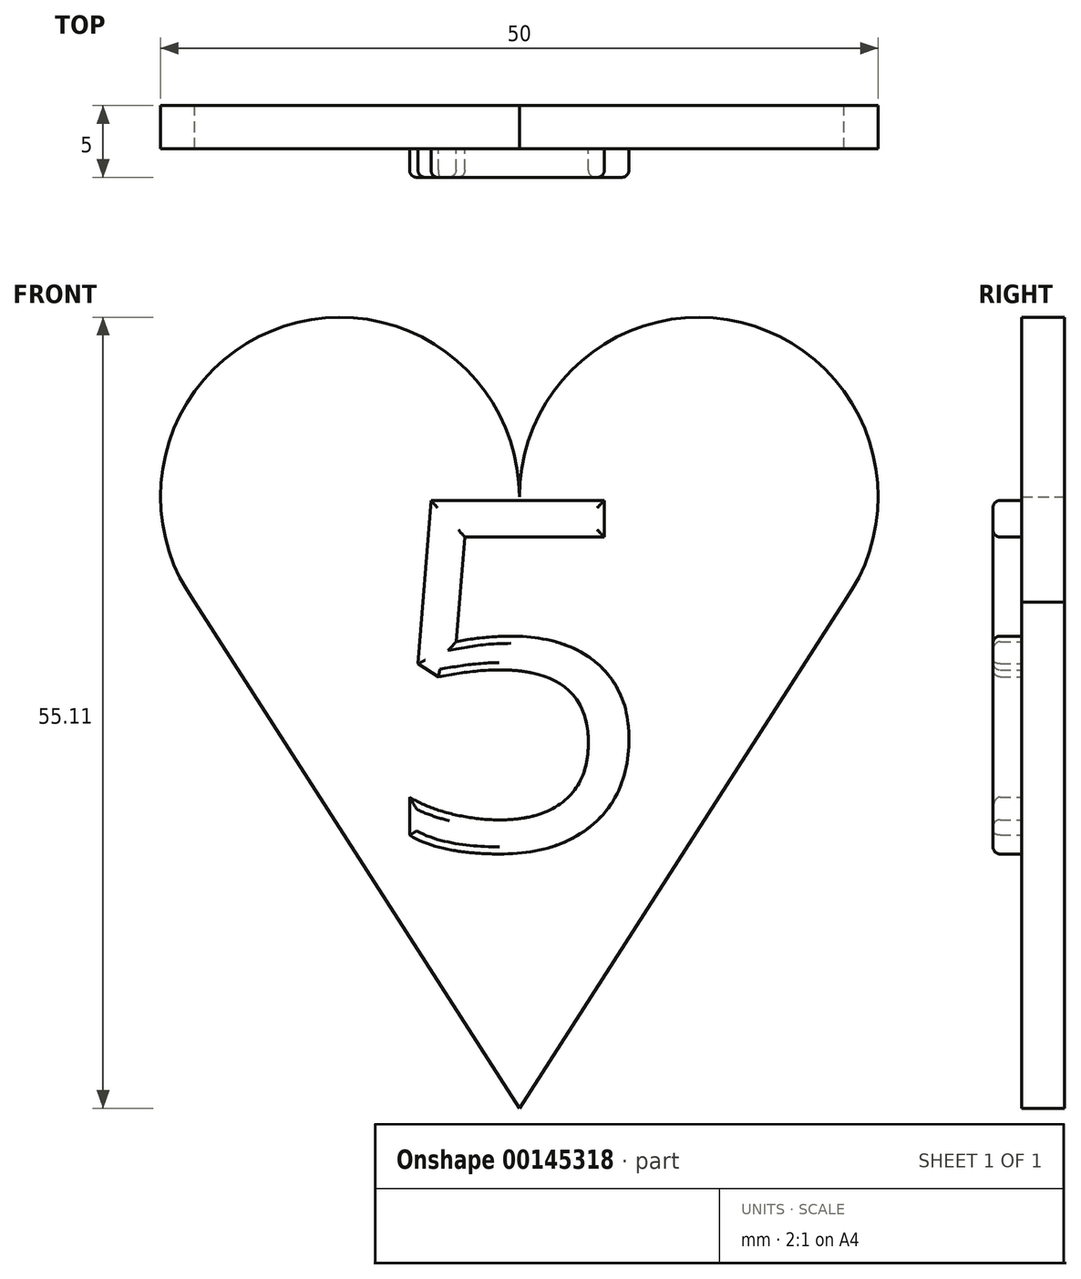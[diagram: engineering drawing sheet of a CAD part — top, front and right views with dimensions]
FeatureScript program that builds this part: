
annotation { "Feature Type Name" : "Feature", "Feature Type Description" : "" }
export const myFeature = defineFeature(function(context is Context, id is Id, definition is map)
    precondition{}
    {
        {
            var Q0;
            Q0=qCreatedBy(makeId("Front.planeOp"),FACE);
            var sketch = newSketch(context, id + "F0", { "sketchPlane" : qUnion([Q0])});
            skCircle(sketch, "E0", {"center": v(-12.5, 12.5) * mm, "radius": 12.5 * mm});
            skCircle(sketch, "E1.MirrorC", {"center": v(12.5, 12.5) * mm, "radius": 12.5 * mm});
            skText(sketch, "E2", { "text": "5\n", "fontName": "OpenSans-Regular.ttf"});
            skLineSegment(sketch, "E3", {"start": v(-23.4, 6.37) * mm, "end": v(0, -30.11) * mm});
            skLineSegment(sketch, "E4.MirrorCS", {"start": v(23.4, 6.37) * mm, "end": v(0, -30.11) * mm});
            const initialGuessF0  = {"E2": [-0.00986, -0.01206, 1, 0, 0.0245]};
            skSetInitialGuess(sketch, initialGuessF0);
            skSolve(sketch);
        }
        {
            var Q0;
            Q0 = qSketchRegion(id + "F0", true);
            var Q1;
            {var subQ0=sQuery(id+"F0.wireOp",EDGE,"E2.sketch_text.stroke-17");var subQ1=sQuery(id+"F0.wireOp",EDGE,"E0");var subQ2=makeQuery(id+"F0.imprint","INTERSECT",VERTEX,{"derivedFrom":[subQ1,subQ0]});Q1=makeQuery(id+"F0.imprint","IMPRINT",FACE,{"disambiguationData":[TD([[makeQuery(id+"F0.imprint","IMPRINT",EDGE,{"disambiguationData":[TD([[subQ2,-1.0]])],"derivedFrom":subQ1}),1.0]])]});}
            extrude(context, id + "F1", {"entities" : qUnion([Q0, Q1]), "depth" : 3 * mm});
        }
        {
            var Q0;
            Q0=makeQuery(id+"F0.imprint","IMPRINT",FACE,{"disambiguationData":[TD([[makeQuery(id+"F0.imprint","IMPRINT",EDGE,{"derivedFrom":sQuery(id+"F0.wireOp",EDGE,"E2.sketch_text.stroke-0")}),-1.0]])]});
            var Q1;
            {var subQ1=sQuery(id+"F0.wireOp",EDGE,"E2.sketch_text.stroke-13");var subQ3=sQuery(id+"F0.wireOp",EDGE,"E0");var subQ10=makeQuery(id+"F0.imprint","INTERSECT",VERTEX,{"derivedFrom":[subQ3,subQ1]});Q1=makeQuery(id+"F0.imprint","IMPRINT",FACE,{"disambiguationData":[TD([[makeQuery(id+"F0.imprint","IMPRINT",EDGE,{"disambiguationData":[TD([[subQ10,-1.0]])],"derivedFrom":subQ3}),1.0]])]});}
            var Q2;
            {var subQ5=sQuery(id+"F0.wireOp",EDGE,"E2.sketch_text.stroke-15");Q2=makeQuery(id+"F0.imprint","IMPRINT",FACE,{"disambiguationData":[TD([[makeQuery(id+"F0.imprint","IMPRINT",EDGE,{"derivedFrom":subQ5}),-1.0]])]});}
            var Q3;
            {var subQ0=sQuery(id+"F0.wireOp",EDGE,"E2.sketch_text.stroke-16");var subQ1=sQuery(id+"F0.wireOp",EDGE,"E0");var subQ2=makeQuery(id+"F0.imprint","INTERSECT",VERTEX,{"derivedFrom":[subQ1,subQ0]});Q3=makeQuery(id+"F0.imprint","IMPRINT",FACE,{"disambiguationData":[TD([[makeQuery(id+"F0.imprint","IMPRINT",EDGE,{"disambiguationData":[TD([[subQ2,-1.0]])],"derivedFrom":subQ1}),-1.0]])]});}
            extrude(context, id + "F2", {"entities" : qUnion([Q0, Q1, Q2, Q3]), "operationType" : NewBodyOperationType.ADD, "depth" : 5 * mm});
        }
        {
            var Q0;
            Q0=makeQuery(id+"F2.opExtrude","CAP_EDGE",EDGE,{"disambiguationData":[OSD([sQuery(id+"F0.wireOp",EDGE,"E2.sketch_text.stroke-14")])],"isStart":false});
            var Q1;
            Q1=makeQuery(id+"F2.opExtrude","CAP_EDGE",EDGE,{"disambiguationData":[OSD([sQuery(id+"F0.wireOp",EDGE,"E2.sketch_text.stroke-15")])],"isStart":false});
            var Q2;
            Q2=makeQuery(id+"F2.opExtrude","CAP_EDGE",EDGE,{"disambiguationData":[OSD([sQuery(id+"F0.wireOp",EDGE,"E2.sketch_text.stroke-16")])],"isStart":false});
            var Q3;
            Q3=makeQuery(id+"F2.opExtrude","CAP_EDGE",EDGE,{"disambiguationData":[OSD([sQuery(id+"F0.wireOp",EDGE,"E2.sketch_text.stroke-17")])],"isStart":false});
            var Q4;
            Q4=makeQuery(id+"F2.opExtrude","CAP_EDGE",EDGE,{"disambiguationData":[OSD([sQuery(id+"F0.wireOp",EDGE,"E2.sketch_text.stroke-18")])],"isStart":false});
            var Q5;
            Q5=makeQuery(id+"F2.opExtrude","CAP_EDGE",EDGE,{"disambiguationData":[OSD([sQuery(id+"F0.wireOp",EDGE,"E2.sketch_text.stroke-0")])],"isStart":false});
            var Q6;
            Q6=makeQuery(id+"F2.opExtrude","CAP_EDGE",EDGE,{"disambiguationData":[OSD([sQuery(id+"F0.wireOp",EDGE,"E2.sketch_text.stroke-1")])],"isStart":false});
            var Q7;
            Q7=makeQuery(id+"F2.opExtrude","CAP_EDGE",EDGE,{"disambiguationData":[OSD([sQuery(id+"F0.wireOp",EDGE,"E2.sketch_text.stroke-5")])],"isStart":false});
            var Q8;
            Q8=makeQuery(id+"F2.opExtrude","CAP_EDGE",EDGE,{"disambiguationData":[OSD([sQuery(id+"F0.wireOp",EDGE,"E2.sketch_text.stroke-7")])],"isStart":false});
            var Q9;
            Q9=makeQuery(id+"F2.opExtrude","CAP_EDGE",EDGE,{"disambiguationData":[OSD([sQuery(id+"F0.wireOp",EDGE,"E2.sketch_text.stroke-13")])],"isStart":false});
            var Q10;
            Q10=makeQuery(id+"F1.opExtrude","CAP_EDGE",EDGE,{"disambiguationData":[OSD([sQuery(id+"F0.wireOp",EDGE,"E2.sketch_text.stroke-18")])],"isStart":false});
            var Q11;
            Q11=makeQuery(id+"F1.opExtrude","CAP_EDGE",EDGE,{"disambiguationData":[OSD([sQuery(id+"F0.wireOp",EDGE,"E2.sketch_text.stroke-15")])],"isStart":false});
            var Q12;
            Q12=makeQuery(id+"F1.opExtrude","CAP_EDGE",EDGE,{"disambiguationData":[OSD([sQuery(id+"F0.wireOp",EDGE,"E2.sketch_text.stroke-14")])],"isStart":false});
            var Q13;
            Q13=makeQuery(id+"F1.opExtrude","CAP_EDGE",EDGE,{"disambiguationData":[OSD([sQuery(id+"F0.wireOp",EDGE,"E2.sketch_text.stroke-16")])],"isStart":false});
            var Q14;
            Q14=makeQuery(id+"F1.opExtrude","CAP_EDGE",EDGE,{"disambiguationData":[OSD([sQuery(id+"F0.wireOp",EDGE,"E2.sketch_text.stroke-17")])],"isStart":false});
            var Q15;
            Q15=makeQuery(id+"F1.opExtrude","CAP_EDGE",EDGE,{"disambiguationData":[OSD([sQuery(id+"F0.wireOp",EDGE,"E2.sketch_text.stroke-11")])],"isStart":false});
            var Q16;
            Q16=makeQuery(id+"F2.opExtrude","CAP_EDGE",EDGE,{"disambiguationData":[OSD([sQuery(id+"F0.wireOp",EDGE,"E2.sketch_text.stroke-12")])],"isStart":false});
            var Q17;
            Q17=makeQuery(id+"F1.opExtrude","CAP_EDGE",EDGE,{"disambiguationData":[OSD([sQuery(id+"F0.wireOp",EDGE,"E2.sketch_text.stroke-12")])],"isStart":false});
            var Q18;
            Q18=makeQuery(id+"F1.opExtrude","CAP_EDGE",EDGE,{"disambiguationData":[OSD([sQuery(id+"F0.wireOp",EDGE,"E2.sketch_text.stroke-13")])],"isStart":false});
            var Q19;
            Q19=makeQuery(id+"F1.opExtrude","CAP_EDGE",EDGE,{"disambiguationData":[OSD([sQuery(id+"F0.wireOp",EDGE,"E2.sketch_text.stroke-5")])],"isStart":false});
            fillet(context, id + "F3", {"entities" : qUnion([Q0, Q1, Q2, Q3, Q4, Q5, Q6, Q7, Q8, Q9, Q10, Q11, Q12, Q13, Q14, Q15, Q16, Q17, Q18, Q19]), "radius" : 0.5 * mm, "tangentPropagation" : true, "allowEdgeOverflow" : false});
        }
    });
